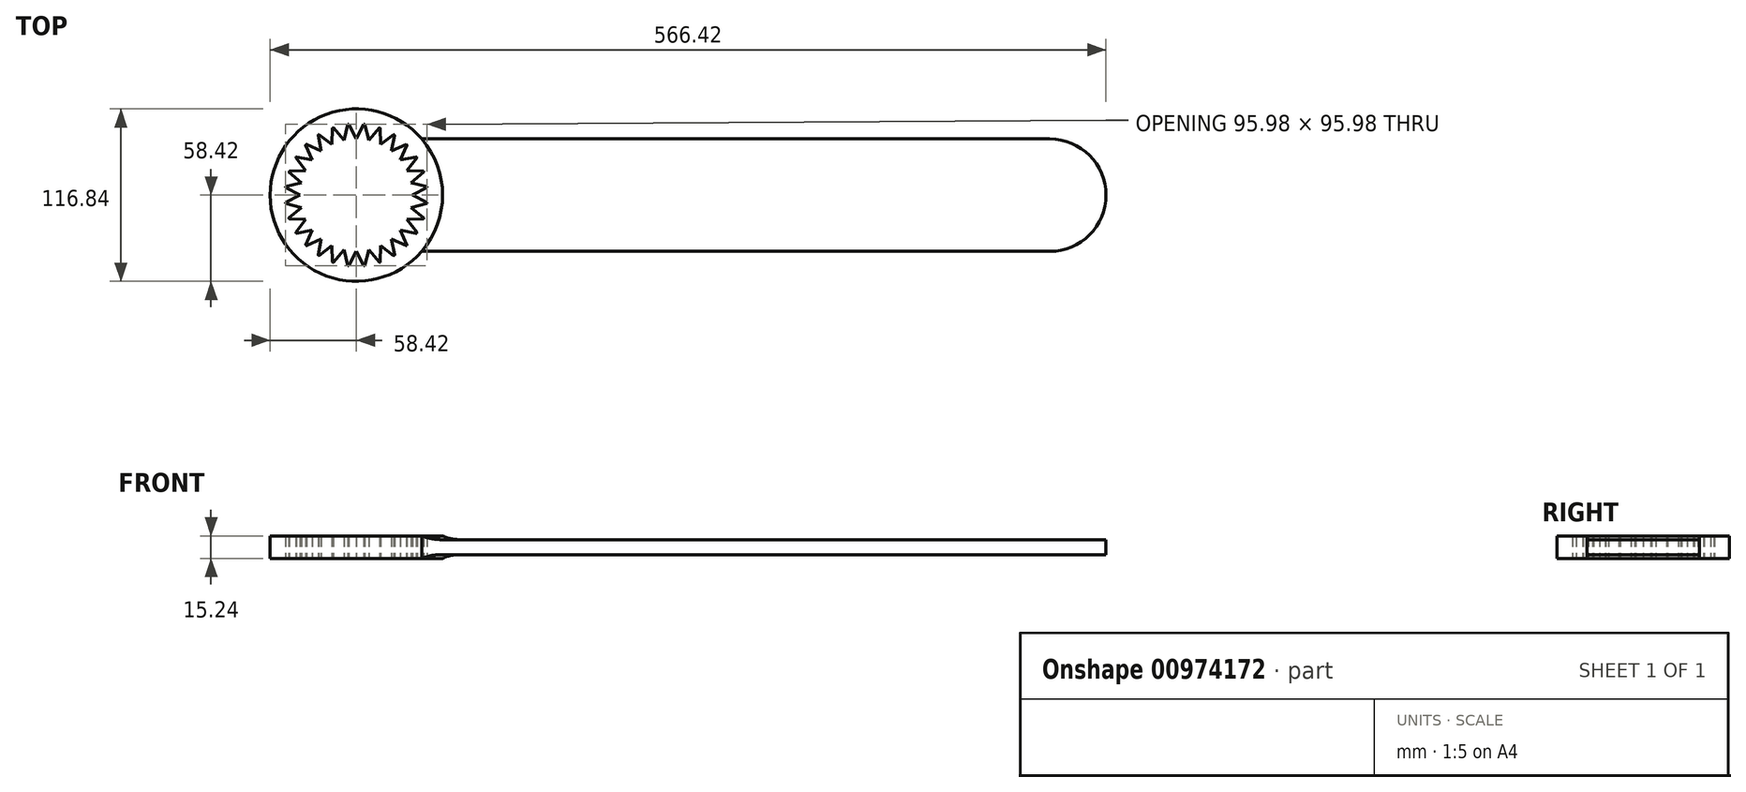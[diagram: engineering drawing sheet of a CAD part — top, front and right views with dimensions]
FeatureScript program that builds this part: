
annotation { "Feature Type Name" : "Feature", "Feature Type Description" : "" }
export const myFeature = defineFeature(function(context is Context, id is Id, definition is map)
    precondition{}
    {
        {
            var Q0;
            Q0=qCreatedBy(makeId("Top.planeOp"),FACE);
            var sketch = newSketch(context, id + "F0", { "sketchPlane" : qUnion([Q0])});
            skCircle(sketch, "E0", {"center": v(0, 0) * mm, "radius": 58.42 * mm});
            skCircle(sketch, "E1", {"center": v(0, 0) * mm, "radius": 48.26 * mm});
            skSolve(sketch);
        }
        {
            var Q0;
            Q0=makeQuery(id+"F0.imprint","IMPRINT",FACE,{"disambiguationData":[TD([[makeQuery(id+"F0.imprint","IMPRINT",EDGE,{"derivedFrom":sQuery(id+"F0.wireOp",EDGE,"E0")}),1.0]])]});
            extrude(context, id + "F1", {"entities" : qUnion([Q0]), "depth" : 15.24 * mm, "offsetDistance" : 25.4 * mm});
        }
        {
            var Q0;
            Q0=qCreatedBy(makeId("Top.planeOp"),FACE);
            cPlane(context, id + "F2", {"entities" : qUnion([Q0]), "cplaneType" : CPlaneType.OFFSET, "offset" : 7.62 * mm, "width" : 152.4 * mm, "height" : 152.4 * mm});
        }
        {
            var Q0;
            Q0=qCreatedBy(id+"F2.planeOp",FACE);
            var sketch = newSketch(context, id + "F3", { "sketchPlane" : qUnion([Q0])});
            skLineSegment(sketch, "E2", {"start": v(44.29, 38.1) * mm, "end": v(469.9, 38.1) * mm});
            skLineSegment(sketch, "E3", {"start": v(469.9, 38.1) * mm, "end": v(469.9, -38.1) * mm, "construction": true});
            skLineSegment(sketch, "E4", {"start": v(469.9, -38.1) * mm, "end": v(44.29, -38.1) * mm});
            skArc(sketch, "E5", {"start": v(469.9, -38.1) * mm, "mid": v(508, 0) * mm, "end": v(469.9, 38.1) * mm});
            skArc(sketch, "E6", {"start": v(44.29, -38.1) * mm, "mid": v(58.39, 0) * mm, "end": v(44.29, 38.1) * mm});
            skSolve(sketch);
        }
        {
            var Q0;
            Q0=makeQuery(id+"F3.imprint","IMPRINT",FACE,{"disambiguationData":[TD([[makeQuery(id+"F3.imprint","IMPRINT",EDGE,{"derivedFrom":sQuery(id+"F3.wireOp",EDGE,"E2")}),-1.0]])]});
            extrude(context, id + "F4", {"entities" : qUnion([Q0]), "operationType" : NewBodyOperationType.ADD, "endBound" : BoundingType.SYMMETRIC, "depth" : 10.16 * mm, "offsetDistance" : 25.4 * mm});
        }
        {
            var Q0;
            Q0=qCreatedBy(id+"F2.planeOp",FACE);
            var sketch = newSketch(context, id + "F5", { "sketchPlane" : qUnion([Q0])});
            skCircle(sketch, "E7", {"center": v(0, 0) * mm, "radius": 38.1 * mm});
            skLineSegment(sketch, "E8", {"start": v(0, 0) * mm, "end": v(0, 48.26) * mm, "construction": true});
            skLineSegment(sketch, "E9", {"start": v(-5.08, 48) * mm, "end": v(0, 38.1) * mm});
            skLineSegment(sketch, "E10", {"start": v(0, 38.1) * mm, "end": v(5.08, 48) * mm});
            skArc(sketch, "E11", {"start": v(5.08, 48) * mm, "mid": v(0, 48.26) * mm, "end": v(-5.08, 48) * mm});
            skLineSegment(sketch, "E12.1.0", {"start": v(-8.48, 37.14) * mm, "end": v(-5.73, 47.92) * mm});
            skLineSegment(sketch, "E12.1.1", {"start": v(-15.63, 45.66) * mm, "end": v(-8.48, 37.14) * mm});
            skArc(sketch, "E12.1.2", {"start": v(-5.73, 47.92) * mm, "mid": v(-10.74, 47.05) * mm, "end": v(-15.63, 45.66) * mm});
            skLineSegment(sketch, "E12.2.0", {"start": v(-16.53, 34.33) * mm, "end": v(-16.25, 45.44) * mm});
            skLineSegment(sketch, "E12.2.1", {"start": v(-25.4, 41.04) * mm, "end": v(-16.53, 34.33) * mm});
            skArc(sketch, "E12.2.2", {"start": v(-16.25, 45.44) * mm, "mid": v(-20.94, 43.48) * mm, "end": v(-25.4, 41.04) * mm});
            skLineSegment(sketch, "E12.3.0", {"start": v(-23.75, 29.79) * mm, "end": v(-25.95, 40.69) * mm});
            skLineSegment(sketch, "E12.3.1", {"start": v(-33.9, 34.35) * mm, "end": v(-23.75, 29.79) * mm});
            skArc(sketch, "E12.3.2", {"start": v(-25.95, 40.69) * mm, "mid": v(-30.09, 37.73) * mm, "end": v(-33.9, 34.35) * mm});
            skLineSegment(sketch, "E12.4.0", {"start": v(-29.79, 23.75) * mm, "end": v(-34.35, 33.9) * mm});
            skLineSegment(sketch, "E12.4.1", {"start": v(-40.69, 25.95) * mm, "end": v(-29.79, 23.75) * mm});
            skArc(sketch, "E12.4.2", {"start": v(-34.35, 33.9) * mm, "mid": v(-37.73, 30.09) * mm, "end": v(-40.69, 25.95) * mm});
            skLineSegment(sketch, "E12.5.0", {"start": v(-34.33, 16.53) * mm, "end": v(-41.04, 25.4) * mm});
            skLineSegment(sketch, "E12.5.1", {"start": v(-45.44, 16.25) * mm, "end": v(-34.33, 16.53) * mm});
            skArc(sketch, "E12.5.2", {"start": v(-41.04, 25.4) * mm, "mid": v(-43.48, 20.94) * mm, "end": v(-45.44, 16.25) * mm});
            skLineSegment(sketch, "E12.6.0", {"start": v(-37.14, 8.48) * mm, "end": v(-45.66, 15.63) * mm});
            skLineSegment(sketch, "E12.6.1", {"start": v(-47.92, 5.73) * mm, "end": v(-37.14, 8.48) * mm});
            skArc(sketch, "E12.6.2", {"start": v(-45.66, 15.63) * mm, "mid": v(-47.05, 10.74) * mm, "end": v(-47.92, 5.73) * mm});
            skLineSegment(sketch, "E12.7.0", {"start": v(-38.1, 0) * mm, "end": v(-48, 5.08) * mm});
            skLineSegment(sketch, "E12.7.1", {"start": v(-48, -5.08) * mm, "end": v(-38.1, 0) * mm});
            skArc(sketch, "E12.7.2", {"start": v(-48, 5.08) * mm, "mid": v(-48.26, 0) * mm, "end": v(-48, -5.08) * mm});
            skLineSegment(sketch, "E12.8.0", {"start": v(-37.14, -8.48) * mm, "end": v(-47.92, -5.73) * mm});
            skLineSegment(sketch, "E12.8.1", {"start": v(-45.66, -15.63) * mm, "end": v(-37.14, -8.48) * mm});
            skArc(sketch, "E12.8.2", {"start": v(-47.92, -5.73) * mm, "mid": v(-47.05, -10.74) * mm, "end": v(-45.66, -15.63) * mm});
            skLineSegment(sketch, "E12.9.0", {"start": v(-34.33, -16.53) * mm, "end": v(-45.44, -16.25) * mm});
            skLineSegment(sketch, "E12.9.1", {"start": v(-41.04, -25.4) * mm, "end": v(-34.33, -16.53) * mm});
            skArc(sketch, "E12.9.2", {"start": v(-45.44, -16.25) * mm, "mid": v(-43.48, -20.94) * mm, "end": v(-41.04, -25.4) * mm});
            skLineSegment(sketch, "E12.10.0", {"start": v(-29.79, -23.75) * mm, "end": v(-40.69, -25.95) * mm});
            skLineSegment(sketch, "E12.10.1", {"start": v(-34.35, -33.9) * mm, "end": v(-29.79, -23.75) * mm});
            skArc(sketch, "E12.10.2", {"start": v(-40.69, -25.95) * mm, "mid": v(-37.73, -30.09) * mm, "end": v(-34.35, -33.9) * mm});
            skLineSegment(sketch, "E12.11.0", {"start": v(-23.75, -29.79) * mm, "end": v(-33.9, -34.35) * mm});
            skLineSegment(sketch, "E12.11.1", {"start": v(-25.95, -40.69) * mm, "end": v(-23.75, -29.79) * mm});
            skArc(sketch, "E12.11.2", {"start": v(-33.9, -34.35) * mm, "mid": v(-30.09, -37.73) * mm, "end": v(-25.95, -40.69) * mm});
            skLineSegment(sketch, "E12.12.0", {"start": v(-16.53, -34.33) * mm, "end": v(-25.4, -41.04) * mm});
            skLineSegment(sketch, "E12.12.1", {"start": v(-16.25, -45.44) * mm, "end": v(-16.53, -34.33) * mm});
            skArc(sketch, "E12.12.2", {"start": v(-25.4, -41.04) * mm, "mid": v(-20.94, -43.48) * mm, "end": v(-16.25, -45.44) * mm});
            skLineSegment(sketch, "E12.13.0", {"start": v(-8.48, -37.14) * mm, "end": v(-15.63, -45.66) * mm});
            skLineSegment(sketch, "E12.13.1", {"start": v(-5.73, -47.92) * mm, "end": v(-8.48, -37.14) * mm});
            skArc(sketch, "E12.13.2", {"start": v(-15.63, -45.66) * mm, "mid": v(-10.74, -47.05) * mm, "end": v(-5.73, -47.92) * mm});
            skLineSegment(sketch, "E12.14.0", {"start": v(0, -38.1) * mm, "end": v(-5.08, -48) * mm});
            skLineSegment(sketch, "E12.14.1", {"start": v(5.08, -48) * mm, "end": v(0, -38.1) * mm});
            skArc(sketch, "E12.14.2", {"start": v(-5.08, -48) * mm, "mid": v(0, -48.26) * mm, "end": v(5.08, -48) * mm});
            skLineSegment(sketch, "E12.15.0", {"start": v(8.48, -37.14) * mm, "end": v(5.73, -47.92) * mm});
            skLineSegment(sketch, "E12.15.1", {"start": v(15.63, -45.66) * mm, "end": v(8.48, -37.14) * mm});
            skArc(sketch, "E12.15.2", {"start": v(5.73, -47.92) * mm, "mid": v(10.74, -47.05) * mm, "end": v(15.63, -45.66) * mm});
            skLineSegment(sketch, "E12.16.0", {"start": v(16.53, -34.33) * mm, "end": v(16.25, -45.44) * mm});
            skLineSegment(sketch, "E12.16.1", {"start": v(25.4, -41.04) * mm, "end": v(16.53, -34.33) * mm});
            skArc(sketch, "E12.16.2", {"start": v(16.25, -45.44) * mm, "mid": v(20.94, -43.48) * mm, "end": v(25.4, -41.04) * mm});
            skLineSegment(sketch, "E12.17.0", {"start": v(23.75, -29.79) * mm, "end": v(25.95, -40.69) * mm});
            skLineSegment(sketch, "E12.17.1", {"start": v(33.9, -34.35) * mm, "end": v(23.75, -29.79) * mm});
            skArc(sketch, "E12.17.2", {"start": v(25.95, -40.69) * mm, "mid": v(30.09, -37.73) * mm, "end": v(33.9, -34.35) * mm});
            skLineSegment(sketch, "E12.18.0", {"start": v(29.79, -23.75) * mm, "end": v(34.35, -33.9) * mm});
            skLineSegment(sketch, "E12.18.1", {"start": v(40.69, -25.95) * mm, "end": v(29.79, -23.75) * mm});
            skArc(sketch, "E12.18.2", {"start": v(34.35, -33.9) * mm, "mid": v(37.73, -30.09) * mm, "end": v(40.69, -25.95) * mm});
            skLineSegment(sketch, "E12.19.0", {"start": v(34.33, -16.53) * mm, "end": v(41.04, -25.4) * mm});
            skLineSegment(sketch, "E12.19.1", {"start": v(45.44, -16.25) * mm, "end": v(34.33, -16.53) * mm});
            skArc(sketch, "E12.19.2", {"start": v(41.04, -25.4) * mm, "mid": v(43.48, -20.94) * mm, "end": v(45.44, -16.25) * mm});
            skLineSegment(sketch, "E12.20.0", {"start": v(37.14, -8.48) * mm, "end": v(45.66, -15.63) * mm});
            skLineSegment(sketch, "E12.20.1", {"start": v(47.92, -5.73) * mm, "end": v(37.14, -8.48) * mm});
            skArc(sketch, "E12.20.2", {"start": v(45.66, -15.63) * mm, "mid": v(47.05, -10.74) * mm, "end": v(47.92, -5.73) * mm});
            skLineSegment(sketch, "E12.21.0", {"start": v(38.1, 0) * mm, "end": v(48, -5.08) * mm});
            skLineSegment(sketch, "E12.21.1", {"start": v(48, 5.08) * mm, "end": v(38.1, 0) * mm});
            skArc(sketch, "E12.21.2", {"start": v(48, -5.08) * mm, "mid": v(48.26, 0) * mm, "end": v(48, 5.08) * mm});
            skLineSegment(sketch, "E12.22.0", {"start": v(37.14, 8.48) * mm, "end": v(47.92, 5.73) * mm});
            skLineSegment(sketch, "E12.22.1", {"start": v(45.66, 15.63) * mm, "end": v(37.14, 8.48) * mm});
            skArc(sketch, "E12.22.2", {"start": v(47.92, 5.73) * mm, "mid": v(47.05, 10.74) * mm, "end": v(45.66, 15.63) * mm});
            skLineSegment(sketch, "E12.23.0", {"start": v(34.33, 16.53) * mm, "end": v(45.44, 16.25) * mm});
            skLineSegment(sketch, "E12.23.1", {"start": v(41.04, 25.4) * mm, "end": v(34.33, 16.53) * mm});
            skArc(sketch, "E12.23.2", {"start": v(45.44, 16.25) * mm, "mid": v(43.48, 20.94) * mm, "end": v(41.04, 25.4) * mm});
            skLineSegment(sketch, "E12.24.0", {"start": v(29.79, 23.75) * mm, "end": v(40.69, 25.95) * mm});
            skLineSegment(sketch, "E12.24.1", {"start": v(34.35, 33.9) * mm, "end": v(29.79, 23.75) * mm});
            skArc(sketch, "E12.24.2", {"start": v(40.69, 25.95) * mm, "mid": v(37.73, 30.09) * mm, "end": v(34.35, 33.9) * mm});
            skLineSegment(sketch, "E12.25.0", {"start": v(23.75, 29.79) * mm, "end": v(33.9, 34.35) * mm});
            skLineSegment(sketch, "E12.25.1", {"start": v(25.95, 40.69) * mm, "end": v(23.75, 29.79) * mm});
            skArc(sketch, "E12.25.2", {"start": v(33.9, 34.35) * mm, "mid": v(30.09, 37.73) * mm, "end": v(25.95, 40.69) * mm});
            skLineSegment(sketch, "E12.26.0", {"start": v(16.53, 34.33) * mm, "end": v(25.4, 41.04) * mm});
            skLineSegment(sketch, "E12.26.1", {"start": v(16.25, 45.44) * mm, "end": v(16.53, 34.33) * mm});
            skArc(sketch, "E12.26.2", {"start": v(25.4, 41.04) * mm, "mid": v(20.94, 43.48) * mm, "end": v(16.25, 45.44) * mm});
            skLineSegment(sketch, "E12.27.0", {"start": v(8.48, 37.14) * mm, "end": v(15.63, 45.66) * mm});
            skLineSegment(sketch, "E12.27.1", {"start": v(5.73, 47.92) * mm, "end": v(8.48, 37.14) * mm});
            skArc(sketch, "E12.27.2", {"start": v(15.63, 45.66) * mm, "mid": v(10.74, 47.05) * mm, "end": v(5.73, 47.92) * mm});
            skSolve(sketch);
        }
        {
            var Q0;
            Q0=makeQuery(id+"F5.imprint","IMPRINT",FACE,{"disambiguationData":[TD([[makeQuery(id+"F5.imprint","IMPRINT",EDGE,{"derivedFrom":sQuery(id+"F5.wireOp",EDGE,"E12.1.0")}),1.0]])]});
            var Q1;
            Q1=makeQuery(id+"F5.imprint","IMPRINT",FACE,{"disambiguationData":[TD([[makeQuery(id+"F5.imprint","IMPRINT",EDGE,{"derivedFrom":sQuery(id+"F5.wireOp",EDGE,"E9")}),1.0]])]});
            var Q2;
            Q2=makeQuery(id+"F5.imprint","IMPRINT",FACE,{"disambiguationData":[TD([[makeQuery(id+"F5.imprint","IMPRINT",EDGE,{"derivedFrom":sQuery(id+"F5.wireOp",EDGE,"E12.27.0")}),1.0]])]});
            var Q3;
            Q3=makeQuery(id+"F5.imprint","IMPRINT",FACE,{"disambiguationData":[TD([[makeQuery(id+"F5.imprint","IMPRINT",EDGE,{"derivedFrom":sQuery(id+"F5.wireOp",EDGE,"E12.26.0")}),1.0]])]});
            var Q4;
            Q4=makeQuery(id+"F5.imprint","IMPRINT",FACE,{"disambiguationData":[TD([[makeQuery(id+"F5.imprint","IMPRINT",EDGE,{"derivedFrom":sQuery(id+"F5.wireOp",EDGE,"E12.25.0")}),1.0]])]});
            var Q5;
            Q5=makeQuery(id+"F5.imprint","IMPRINT",FACE,{"disambiguationData":[TD([[makeQuery(id+"F5.imprint","IMPRINT",EDGE,{"derivedFrom":sQuery(id+"F5.wireOp",EDGE,"E12.24.0")}),1.0]])]});
            var Q6;
            Q6=makeQuery(id+"F5.imprint","IMPRINT",FACE,{"disambiguationData":[TD([[makeQuery(id+"F5.imprint","IMPRINT",EDGE,{"derivedFrom":sQuery(id+"F5.wireOp",EDGE,"E12.23.0")}),1.0]])]});
            var Q7;
            Q7=makeQuery(id+"F5.imprint","IMPRINT",FACE,{"disambiguationData":[TD([[makeQuery(id+"F5.imprint","IMPRINT",EDGE,{"derivedFrom":sQuery(id+"F5.wireOp",EDGE,"E12.22.0")}),1.0]])]});
            var Q8;
            Q8=makeQuery(id+"F5.imprint","IMPRINT",FACE,{"disambiguationData":[TD([[makeQuery(id+"F5.imprint","IMPRINT",EDGE,{"derivedFrom":sQuery(id+"F5.wireOp",EDGE,"E12.21.0")}),1.0]])]});
            var Q9;
            Q9=makeQuery(id+"F5.imprint","IMPRINT",FACE,{"disambiguationData":[TD([[makeQuery(id+"F5.imprint","IMPRINT",EDGE,{"derivedFrom":sQuery(id+"F5.wireOp",EDGE,"E12.20.0")}),1.0]])]});
            var Q10;
            Q10=makeQuery(id+"F5.imprint","IMPRINT",FACE,{"disambiguationData":[TD([[makeQuery(id+"F5.imprint","IMPRINT",EDGE,{"derivedFrom":sQuery(id+"F5.wireOp",EDGE,"E12.19.0")}),1.0]])]});
            var Q11;
            Q11=makeQuery(id+"F5.imprint","IMPRINT",FACE,{"disambiguationData":[TD([[makeQuery(id+"F5.imprint","IMPRINT",EDGE,{"derivedFrom":sQuery(id+"F5.wireOp",EDGE,"E12.18.0")}),1.0]])]});
            var Q12;
            Q12=makeQuery(id+"F5.imprint","IMPRINT",FACE,{"disambiguationData":[TD([[makeQuery(id+"F5.imprint","IMPRINT",EDGE,{"derivedFrom":sQuery(id+"F5.wireOp",EDGE,"E12.16.0")}),1.0]])]});
            var Q13;
            Q13=makeQuery(id+"F5.imprint","IMPRINT",FACE,{"disambiguationData":[TD([[makeQuery(id+"F5.imprint","IMPRINT",EDGE,{"derivedFrom":sQuery(id+"F5.wireOp",EDGE,"E12.15.0")}),1.0]])]});
            var Q14;
            Q14=makeQuery(id+"F5.imprint","IMPRINT",FACE,{"disambiguationData":[TD([[makeQuery(id+"F5.imprint","IMPRINT",EDGE,{"derivedFrom":sQuery(id+"F5.wireOp",EDGE,"E12.14.0")}),1.0]])]});
            var Q15;
            Q15=makeQuery(id+"F5.imprint","IMPRINT",FACE,{"disambiguationData":[TD([[makeQuery(id+"F5.imprint","IMPRINT",EDGE,{"derivedFrom":sQuery(id+"F5.wireOp",EDGE,"E12.17.0")}),1.0]])]});
            var Q16;
            Q16=makeQuery(id+"F5.imprint","IMPRINT",FACE,{"disambiguationData":[TD([[makeQuery(id+"F5.imprint","IMPRINT",EDGE,{"derivedFrom":sQuery(id+"F5.wireOp",EDGE,"E12.13.0")}),1.0]])]});
            var Q17;
            Q17=makeQuery(id+"F5.imprint","IMPRINT",FACE,{"disambiguationData":[TD([[makeQuery(id+"F5.imprint","IMPRINT",EDGE,{"derivedFrom":sQuery(id+"F5.wireOp",EDGE,"E12.12.0")}),1.0]])]});
            var Q18;
            Q18=makeQuery(id+"F5.imprint","IMPRINT",FACE,{"disambiguationData":[TD([[makeQuery(id+"F5.imprint","IMPRINT",EDGE,{"derivedFrom":sQuery(id+"F5.wireOp",EDGE,"E12.11.0")}),1.0]])]});
            var Q19;
            Q19=makeQuery(id+"F5.imprint","IMPRINT",FACE,{"disambiguationData":[TD([[makeQuery(id+"F5.imprint","IMPRINT",EDGE,{"derivedFrom":sQuery(id+"F5.wireOp",EDGE,"E12.10.0")}),1.0]])]});
            var Q20;
            Q20=makeQuery(id+"F5.imprint","IMPRINT",FACE,{"disambiguationData":[TD([[makeQuery(id+"F5.imprint","IMPRINT",EDGE,{"derivedFrom":sQuery(id+"F5.wireOp",EDGE,"E12.9.0")}),1.0]])]});
            var Q21;
            Q21=makeQuery(id+"F5.imprint","IMPRINT",FACE,{"disambiguationData":[TD([[makeQuery(id+"F5.imprint","IMPRINT",EDGE,{"derivedFrom":sQuery(id+"F5.wireOp",EDGE,"E12.8.0")}),1.0]])]});
            var Q22;
            Q22=makeQuery(id+"F5.imprint","IMPRINT",FACE,{"disambiguationData":[TD([[makeQuery(id+"F5.imprint","IMPRINT",EDGE,{"derivedFrom":sQuery(id+"F5.wireOp",EDGE,"E12.7.0")}),1.0]])]});
            var Q23;
            Q23=makeQuery(id+"F5.imprint","IMPRINT",FACE,{"disambiguationData":[TD([[makeQuery(id+"F5.imprint","IMPRINT",EDGE,{"derivedFrom":sQuery(id+"F5.wireOp",EDGE,"E12.6.0")}),1.0]])]});
            var Q24;
            Q24=makeQuery(id+"F5.imprint","IMPRINT",FACE,{"disambiguationData":[TD([[makeQuery(id+"F5.imprint","IMPRINT",EDGE,{"derivedFrom":sQuery(id+"F5.wireOp",EDGE,"E12.5.0")}),1.0]])]});
            var Q25;
            Q25=makeQuery(id+"F5.imprint","IMPRINT",FACE,{"disambiguationData":[TD([[makeQuery(id+"F5.imprint","IMPRINT",EDGE,{"derivedFrom":sQuery(id+"F5.wireOp",EDGE,"E12.4.0")}),1.0]])]});
            var Q26;
            Q26=makeQuery(id+"F5.imprint","IMPRINT",FACE,{"disambiguationData":[TD([[makeQuery(id+"F5.imprint","IMPRINT",EDGE,{"derivedFrom":sQuery(id+"F5.wireOp",EDGE,"E12.3.0")}),1.0]])]});
            var Q27;
            Q27=makeQuery(id+"F5.imprint","IMPRINT",FACE,{"disambiguationData":[TD([[makeQuery(id+"F5.imprint","IMPRINT",EDGE,{"derivedFrom":sQuery(id+"F5.wireOp",EDGE,"E12.2.0")}),1.0]])]});
            extrude(context, id + "F6", {"entities" : qUnion([Q0, Q1, Q2, Q3, Q4, Q5, Q6, Q7, Q8, Q9, Q10, Q11, Q12, Q13, Q14, Q15, Q16, Q17, Q18, Q19, Q20, Q21, Q22, Q23, Q24, Q25, Q26, Q27]), "operationType" : NewBodyOperationType.ADD, "endBound" : BoundingType.SYMMETRIC, "depth" : 15.24 * mm, "offsetDistance" : 25.4 * mm});
        }
        {
            var Q0;
            Q0=makeQuery(id+"F4.boolean.opBoolean","INTERSECT",EDGE,{"derivedFrom":[makeQuery(id+"F1.opExtrude","SWEPT_FACE",FACE,{"disambiguationData":[OSD([sQuery(id+"F0.wireOp",EDGE,"E0")])]}),makeQuery(id+"F4.opExtrude","CAP_FACE",FACE,{"disambiguationData":[OSD([sQuery(id+"F3.wireOp",EDGE,"E2"),sQuery(id+"F3.wireOp",EDGE,"E4"),sQuery(id+"F3.wireOp",EDGE,"E5"),sQuery(id+"F3.wireOp",EDGE,"E6")])],"isStart":false})]});
            var Q1;
            Q1=makeQuery(id+"F4.boolean.opBoolean","INTERSECT",EDGE,{"derivedFrom":[makeQuery(id+"F1.opExtrude","SWEPT_FACE",FACE,{"disambiguationData":[OSD([sQuery(id+"F0.wireOp",EDGE,"E0")])]}),makeQuery(id+"F4.opExtrude","CAP_FACE",FACE,{"disambiguationData":[OSD([sQuery(id+"F3.wireOp",EDGE,"E2"),sQuery(id+"F3.wireOp",EDGE,"E4"),sQuery(id+"F3.wireOp",EDGE,"E5"),sQuery(id+"F3.wireOp",EDGE,"E6")])],"isStart":true})]});
            fillet(context, id + "F7", {"entities" : qUnion([Q0, Q1]), "radius" : 25.4 * mm, "tangentPropagation" : true, "allowEdgeOverflow" : false});
        }
    });
